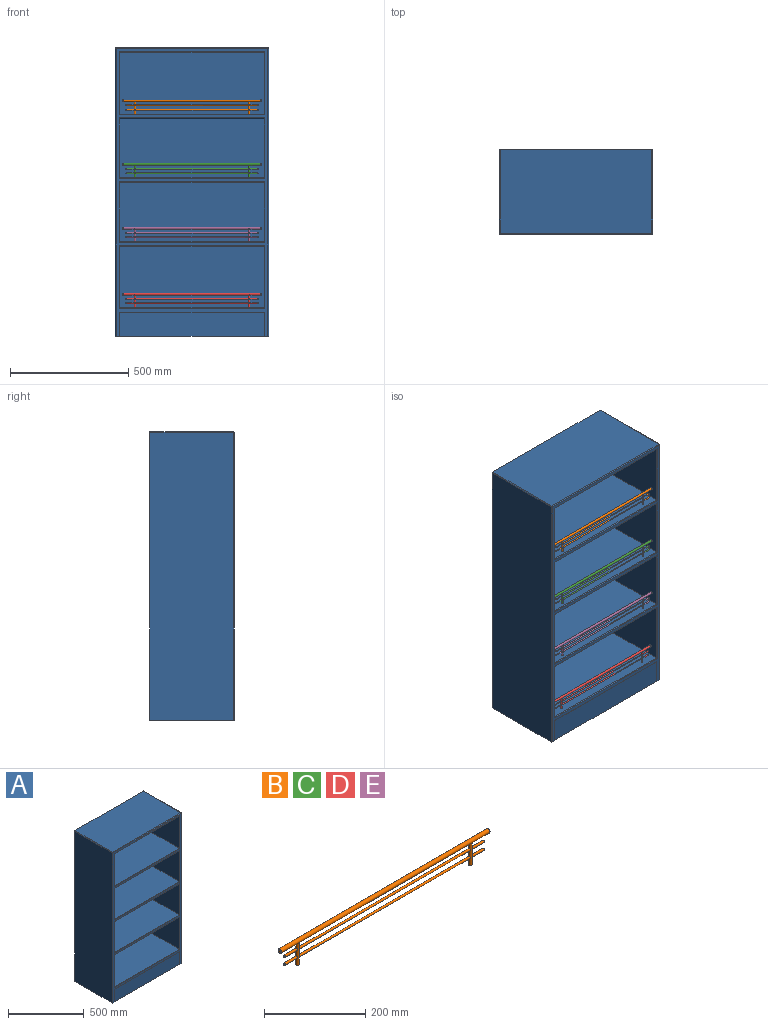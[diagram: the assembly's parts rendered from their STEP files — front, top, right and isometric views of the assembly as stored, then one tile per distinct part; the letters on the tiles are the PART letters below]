
ASSEMBLY  parts=5 mates=4
PART A: 59 faces, bbox 647.7x355.6x1219.2 mm
  f0: plane 333.38x261.53mm, normal (1,0,0), area 87187.9mm2, adj f16,f24,f25,f38
  f1: plane 333.38x261.53mm, normal (-1,0,0), area 87187.9mm2, adj f16,f24,f25,f35
  f2: plane 333.38x250.43mm, normal (1,0,0), area 83487.5mm2, adj f14,f17,f31,f54
  f3: plane 333.38x250.43mm, normal (-1,0,0), area 83487.5mm2, adj f14,f17,f34,f54
  f4: plane 333.38x250.43mm, normal (1,0,0), area 83487.5mm2, adj f12,f15,f39,f55
  f5: plane 333.38x250.43mm, normal (-1,0,0), area 83487.5mm2, adj f12,f15,f42,f55
  f6: plane 333.38x259.96mm, normal (1,0,0), area 86662.9mm2, adj f11,f13,f43,f56
  f7: plane 334.96x101.6mm, normal (1,0,0), area 32701.5mm2, adj f10,f19,f20,f26,f57,f58
  f8: plane 333.38x259.96mm, normal (-1,0,0), area 86662.9mm2, adj f11,f13,f46,f56
  f9: plane 334.96x101.6mm, normal (-1,0,0), area 32701.5mm2, adj f10,f19,f20,f26,f57,f58
  f10: plane 609.6x315.91mm, normal (0,0,-1), area 192580.3mm2, adj f7,f9,f26,f57
  f11: plane 609.6x333.38mm, normal (0,0,1), area 203225.4mm2, adj f6,f8,f45,f56
  f12: plane 609.6x333.38mm, normal (0,0,1), area 203225.4mm2, adj f4,f5,f41,f55
  f13: plane 609.6x333.38mm, normal (0,0,-1), area 203225.4mm2, adj f6,f8,f44,f56
  f14: plane 609.6x333.38mm, normal (0,0,1), area 203225.4mm2, adj f2,f3,f33,f54
  f15: plane 609.6x333.38mm, normal (0,0,-1), area 203225.4mm2, adj f4,f5,f40,f55
  f16: plane 609.6x333.38mm, normal (0,0,1), area 203225.4mm2, adj f0,f1,f25,f36
  f17: plane 609.6x333.38mm, normal (0,0,-1), area 203225.4mm2, adj f2,f3,f32,f54
  f18: plane 101.6x1.59mm, normal (1,0,0), area 161.3mm2, adj f19,f22,f27,f28
  f19: plane 647.7x355.6mm, normal (0,0,-1), area 25156.9mm2, adj f7,f9,f18,f20,f22,f23,f26,f28
  f20: plane 1219.2x647.7mm, normal (0,1,0), area 770316.7mm2, adj f7,f9,f19,f21,f23,f29,f48,f51
  f21: plane 641.35x352.43mm, normal (0,0,1), area 226027.8mm2, adj f20,f48,f50,f51
  f22: plane 1216.03x641.35mm, normal (0,-1,0), area 72600.7mm2, adj f18,f19,f27,f30,f31,f32,f33,f34
  f23: plane 1216.03x352.43mm, normal (-1,0,0), area 428557.6mm2, adj f19,f20,f47,f48
  f24: plane 609.6x333.38mm, normal (0,0,-1), area 203225.4mm2, adj f0,f1,f25,f37
  f25: plane 609.6x261.53mm, normal (0,-1,0), area 159429.4mm2, adj f0,f1,f16,f24
  f26: plane 609.6x101.6mm, normal (0,1,0), area 61935.4mm2, adj f7,f9,f10,f19
  f27: plane 609.6x1.59mm, normal (0,0,-1), area 967.7mm2, adj f18,f22,f28,f30
  f28: plane 609.6x101.6mm, normal (0,-1,0), area 61935.4mm2, adj f18,f19,f27,f30
  f29: plane 1216.03x352.43mm, normal (1,0,0), area 428557.6mm2, adj f19,f20,f51,f53
  f30: plane 101.6x1.59mm, normal (-1,0,0), area 161.3mm2, adj f19,f22,f27,f28
  f31: cylinder r=3.17mm len=256.78mm, axis (0,0,1), area 1260.5mm2, adj f2,f22,f32,f33
  f32: cylinder r=3.17mm len=615.95mm, axis (1,0,0), area 3051.8mm2, adj f17,f22,f31,f34
  f33: cylinder r=3.17mm len=615.95mm, axis (-1,0,0), area 3051.8mm2, adj f14,f22,f31,f34
  f34: cylinder r=3.17mm len=256.78mm, axis (0,0,1), area 1260.5mm2, adj f3,f22,f32,f33
  f35: cylinder r=3.17mm len=267.88mm, axis (0,0,1), area 1315.8mm2, adj f1,f22,f36,f37
  f36: cylinder r=3.17mm len=615.95mm, axis (-1,0,0), area 3051.8mm2, adj f16,f22,f35,f38
  f37: cylinder r=3.17mm len=615.95mm, axis (1,0,0), area 3051.8mm2, adj f22,f24,f35,f38
  f38: cylinder r=3.17mm len=267.88mm, axis (0,0,1), area 1315.8mm2, adj f0,f22,f36,f37
  f39: cylinder r=3.17mm len=256.78mm, axis (0,0,1), area 1260.5mm2, adj f4,f22,f40,f41
  f40: cylinder r=3.17mm len=615.95mm, axis (1,0,0), area 3051.8mm2, adj f15,f22,f39,f42
  f41: cylinder r=3.17mm len=615.95mm, axis (-1,0,0), area 3051.8mm2, adj f12,f22,f39,f42
  f42: cylinder r=3.17mm len=256.78mm, axis (0,0,1), area 1260.5mm2, adj f5,f22,f40,f41
  f43: cylinder r=3.17mm len=266.31mm, axis (0,0,1), area 1308mm2, adj f6,f22,f44,f45
  f44: cylinder r=3.17mm len=615.95mm, axis (1,0,0), area 3051.8mm2, adj f13,f22,f43,f46
  f45: cylinder r=3.17mm len=615.95mm, axis (-1,0,0), area 3051.8mm2, adj f11,f22,f43,f46
  f46: cylinder r=3.17mm len=266.31mm, axis (0,0,1), area 1308mm2, adj f8,f22,f44,f45
  f47: cylinder r=3.17mm len=1216.03mm, axis (0,0,-1), area 6064.7mm2, adj f19,f22,f23,f49
  f48: cylinder r=3.17mm len=352.43mm, axis (0,-1,0), area 1757.6mm2, adj f20,f21,f23,f49
  f49: sphere r=3.17mm, area 15.8mm2, adj f47,f48,f50
  f50: cylinder r=3.17mm len=641.35mm, axis (1,0,0), area 3198.6mm2, adj f21,f22,f49,f52
  f51: cylinder r=3.17mm len=352.43mm, axis (0,1,0), area 1757.6mm2, adj f20,f21,f29,f52
  f52: sphere r=3.17mm, area 15.8mm2, adj f50,f51,f53
  f53: cylinder r=3.17mm len=1216.03mm, axis (0,0,-1), area 6064.7mm2, adj f19,f22,f29,f52
  f54: plane 609.6x250.43mm, normal (0,-1,0), area 152662.9mm2, adj f2,f3,f14,f17
  f55: plane 609.6x250.43mm, normal (0,-1,0), area 152662.9mm2, adj f4,f5,f12,f15
  f56: plane 609.6x259.96mm, normal (0,-1,0), area 158469.4mm2, adj f6,f8,f11,f13
  f57: plane 609.6x69.85mm, normal (0,-1,0), area 42580.6mm2, adj f7,f9,f10,f58
  f58: plane 609.6x19.05mm, normal (0,0,-1), area 11612.9mm2, adj f7,f9,f20,f57
PART B: 23 faces, bbox 584.2x10.3x62.3 mm
  f0: cylinder r=4.76mm len=581.03mm, axis (-1,0,0), area 17318.8mm2, adj f5,f12,f14,f15
  f1: cylinder r=2.37mm len=478.39mm, axis (-1,0,0), area 7121.7mm2, adj f5,f15
  f2: cylinder r=2.37mm len=478.39mm, axis (-1,0,0), area 7121.7mm2, adj f5,f15
  f3: cylinder r=2.37mm len=34.41mm, axis (-1,0,0), area 505mm2, adj f5,f11
  f4: cylinder r=2.37mm len=34.41mm, axis (-1,0,0), area 505mm2, adj f5,f10
  f5: cylinder r=3.17mm len=53.6mm, axis (0,0,-1), area 979.4mm2, adj f0,f1,f2,f3,f4,f6
  f6: plane 6.35x6.35mm, normal (0,0,-1), area 31.7mm2, adj f5
  f7: plane 6.35x6.35mm, normal (1,0,0), area 31.7mm2, adj f12
  f8: plane 1.57x1.57mm, normal (1,0,0), area 1.9mm2, adj f10
  f9: plane 1.58x1.57mm, normal (1,0,0), area 1.9mm2, adj f11
  f10: torus R=0.79mm, axis (1,0,0), area 28.2mm2, adj f4,f8
  f11: torus R=0.79mm, axis (1,0,0), area 28.2mm2, adj f3,f9
  f12: torus R=3.17mm, axis (1,0,0), area 65.6mm2, adj f0,f7
  f13: plane 6.35x6.35mm, normal (-1,0,0), area 31.7mm2, adj f14
  f14: torus R=3.17mm, axis (1,0,0), area 65.6mm2, adj f0,f13
  f15: cylinder r=3.17mm len=53.6mm, axis (0,0,-1), area 979.4mm2, adj f0,f1,f2,f16,f19,f22
  f16: plane 6.35x6.35mm, normal (0,0,-1), area 31.7mm2, adj f15
  f17: plane 1.57x1.57mm, normal (-1,0,0), area 1.9mm2, adj f18
  f18: torus R=0.79mm, axis (1,0,0), area 28.2mm2, adj f17,f19
  f19: cylinder r=2.37mm len=34.41mm, axis (-1,0,0), area 505mm2, adj f15,f18
  f20: plane 1.58x1.57mm, normal (-1,0,0), area 1.9mm2, adj f21
  f21: torus R=0.79mm, axis (1,0,0), area 28.2mm2, adj f20,f22
  f22: cylinder r=2.37mm len=34.41mm, axis (-1,0,0), area 505mm2, adj f15,f21
PART C: same geometry as B
PART D: same geometry as B
PART E: same geometry as B
PLACE A t=(370.98,349.78,-77.07)mm
PLACE B t=(694.83,191.03,251.95)mm
PLACE C t=(694.83,191.03,-17.53)mm
PLACE D t=(694.83,197.38,-566.02)mm
PLACE E t=(694.83,191.03,-287.01)mm
MATE fastened D.f6 <-> A.f11  axis (0,0,1) through (694.83,197.38,-566.02)mm
MATE fastened E.f6 <-> A.f12  axis (0,0,1) through (694.83,191.03,-287.01)mm
MATE fastened B.f6 <-> A.f16  axis (0,0,1) through (694.83,191.03,251.95)mm
MATE fastened C.f6 <-> A.f14  axis (0,0,1) through (694.83,191.03,-17.53)mm
